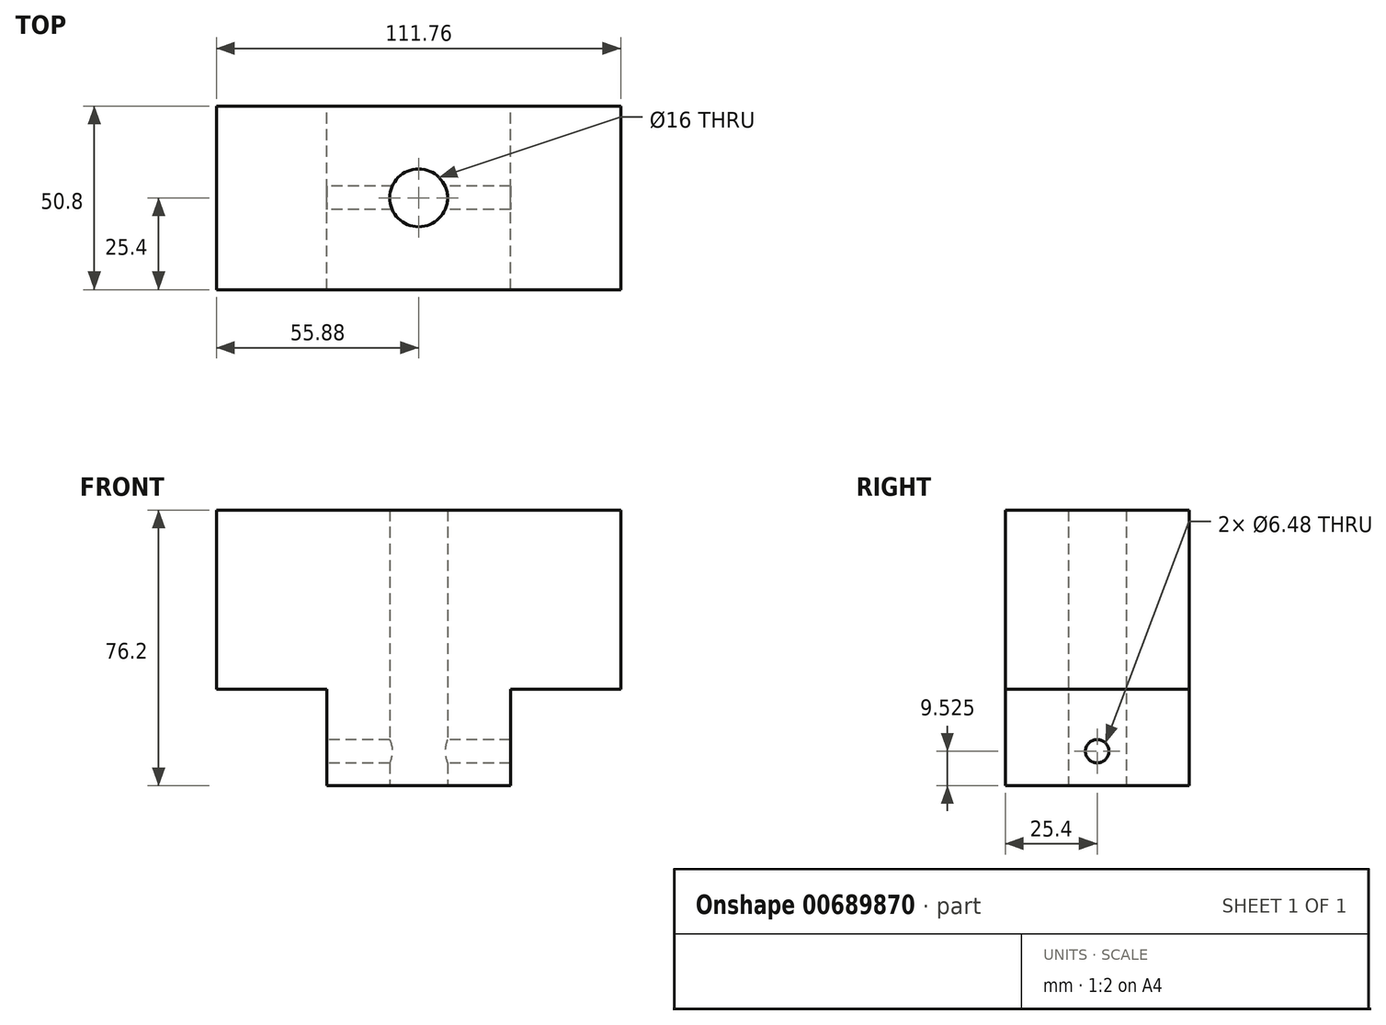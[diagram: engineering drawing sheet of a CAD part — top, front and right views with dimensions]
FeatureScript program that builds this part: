
annotation { "Feature Type Name" : "Feature", "Feature Type Description" : "" }
export const myFeature = defineFeature(function(context is Context, id is Id, definition is map)
    precondition{}
    {
        {
            var Q0;
            Q0=qCreatedBy(makeId("Top.planeOp"),FACE);
            var sketch = newSketch(context, id + "F0", { "sketchPlane" : qUnion([Q0])});
            skLineSegment(sketch, "E0.bottom", {"start": v(-25.4, -25.4) * mm, "end": v(25.4, -25.4) * mm});
            skLineSegment(sketch, "E0.top", {"start": v(-25.4, 25.4) * mm, "end": v(25.4, 25.4) * mm});
            skLineSegment(sketch, "E0.left", {"start": v(-25.4, -25.4) * mm, "end": v(-25.4, 25.4) * mm});
            skLineSegment(sketch, "E0.right", {"start": v(25.4, -25.4) * mm, "end": v(25.4, 25.4) * mm});
            skPoint(sketch, "E0.middle", {"position": v(0, 0) * mm});
            skCircle(sketch, "E1", {"center": v(0, 0) * mm, "radius": 8 * mm});
            skSolve(sketch);
        }
        {
            var Q0;
            Q0=makeQuery(id+"F0.imprint","IMPRINT",FACE,{"disambiguationData":[TD([[makeQuery(id+"F0.imprint","IMPRINT",EDGE,{"derivedFrom":sQuery(id+"F0.wireOp",EDGE,"E0.bottom")}),1.0]])]});
            extrude(context, id + "F1", {"entities" : qUnion([Q0]), "depth" : 26.67 * mm, "offsetDistance" : 25.4 * mm});
        }
        {
            var Q0;
            Q0=makeQuery(id+"F1.opExtrude","CAP_FACE",FACE,{"disambiguationData":[OSD([sQuery(id+"F0.wireOp",EDGE,"E0.bottom"),sQuery(id+"F0.wireOp",EDGE,"E0.top"),sQuery(id+"F0.wireOp",EDGE,"E0.left"),sQuery(id+"F0.wireOp",EDGE,"E0.right"),sQuery(id+"F0.wireOp",EDGE,"E1")])],"isStart":false});
            var sketch = newSketch(context, id + "F2", { "sketchPlane" : qUnion([Q0])});
            skLineSegment(sketch, "E2.bottom", {"start": v(-55.88, -25.4) * mm, "end": v(55.88, -25.4) * mm});
            skLineSegment(sketch, "E2.top", {"start": v(-55.88, 25.4) * mm, "end": v(55.88, 25.4) * mm});
            skLineSegment(sketch, "E2.left", {"start": v(-55.88, -25.4) * mm, "end": v(-55.88, 25.4) * mm});
            skLineSegment(sketch, "E2.right", {"start": v(55.88, -25.4) * mm, "end": v(55.88, 25.4) * mm});
            skPoint(sketch, "E2.middle", {"position": v(0, 0) * mm});
            skSolve(sketch);
        }
        {
            var Q0;
            {var subQ2=sQuery(id+"F2.wireOp",EDGE,"E2.left");Q0=makeQuery(id+"F2.imprint","IMPRINT",FACE,{"disambiguationData":[TD([[makeQuery(id+"F2.imprint","IMPRINT",EDGE,{"derivedFrom":subQ2}),-1.0]])]});}
            var Q1;
            {var subQ0=makeQuery(id+"F1.opExtrude","CAP_EDGE",EDGE,{"disambiguationData":[OSD([sQuery(id+"F0.wireOp",EDGE,"E0.left")])],"isStart":false});Q1=makeQuery(id+"F2.imprint","IMPRINT",FACE,{"disambiguationData":[TD([[makeQuery(id+"F2.imprint","IMPRINT",EDGE,{"derivedFrom":subQ0}),-1.0]])]});}
            var Q2;
            {var subQ2=sQuery(id+"F2.wireOp",EDGE,"E2.right");Q2=makeQuery(id+"F2.imprint","IMPRINT",FACE,{"disambiguationData":[TD([[makeQuery(id+"F2.imprint","IMPRINT",EDGE,{"derivedFrom":subQ2}),1.0]])]});}
            extrude(context, id + "F3", {"entities" : qUnion([Q0, Q1, Q2]), "operationType" : NewBodyOperationType.ADD, "depth" : 49.53 * mm, "offsetDistance" : 25.4 * mm});
        }
        {
            var Q0;
            Q0=makeQuery(id+"F1.opExtrude","SWEPT_FACE",FACE,{"disambiguationData":[OSD([sQuery(id+"F0.wireOp",EDGE,"E0.left")])]});
            var sketch = newSketch(context, id + "F4", { "sketchPlane" : qUnion([Q0])});
            skCircle(sketch, "E3", {"center": v(0, 9.53) * mm, "radius": 3.24 * mm});
            skSolve(sketch);
        }
        {
            var Q0;
            Q0=makeQuery(id+"F4.imprint","IMPRINT",FACE,{"disambiguationData":[TD([[makeQuery(id+"F4.imprint","IMPRINT",EDGE,{"derivedFrom":sQuery(id+"F4.wireOp",EDGE,"E3")}),1.0]])]});
            extrude(context, id + "F5", {"entities" : qUnion([Q0]), "operationType" : NewBodyOperationType.REMOVE, "endBound" : BoundingType.THROUGH_ALL, "oppositeDirection" : true, "depth" : 25.4 * mm, "offsetDistance" : 25.4 * mm});
        }
    });
